# Revit family: Magnuson-KrokHJH-CoatHookStrip-1
name_source: partatom
category: Furniture
units: mm (PartAtom-declared; Revit-internal decimal feet)

## family parameters
Cut with Voids When Loaded = No
Host = Face
Room Calculation Point = No
Shared = No

## types (4) — shared parameters
Assembly Code = E2020200
Default Elevation = 48"
Frame Finish = MAG - Textured painted steel
Hook Finish = MAG - Plastic Black
Keynote = 12500
Low Emitting Finish = Yes
Low Emitting Material = Yes
Manufacturer = Magnuson Group
Revit Model Built By = https://servex-us.com
Salvage or Reuse = Yes
URL = www.magnusongroup.com
zero-valued in all types: Percentage of Recycled Content

## per-type parameters (varying)
| type | Description | Dist Hook | Hook Qty | Product Documentation Link | Support-1 | Support-2 | Type Comments | Width |
| KROK HJH-30 | Textured painted steel hook strip with two matching plastic coat hooks. | 3 5/32" | 2 | https://magnusongroup.com | Yes | No | Coat Hook Strip | 11 13/16" |
| KROK HJH-90 | Textured painted steel hook strip with eight matching plastic coat hooks. | 3 5/32" | 8 | https://magnusongroup.com | Yes | No | Coat Hook Strip | 35 13/16" |
| KROK HJH-60 | Textured painted steel hook strip with five matching plastic coat hooks. | 3 5/32" | 5 | https://magnusongroup.com | Yes | Yes | Coat Hook Strip | 23 13/16" |
| KROK HJH-10 | Front mount coat hook with back plate and matching plastic hook | 1 11/16" | 2 | https://www.magnusongroup.com | No | Yes | Coat Hook | 3 3/8" |

note: column(s) folded — value = type name in every type: Model

## geometry (parser evidence)
native form markers: Sweep x5
no freeform markers — native parametric forms only
